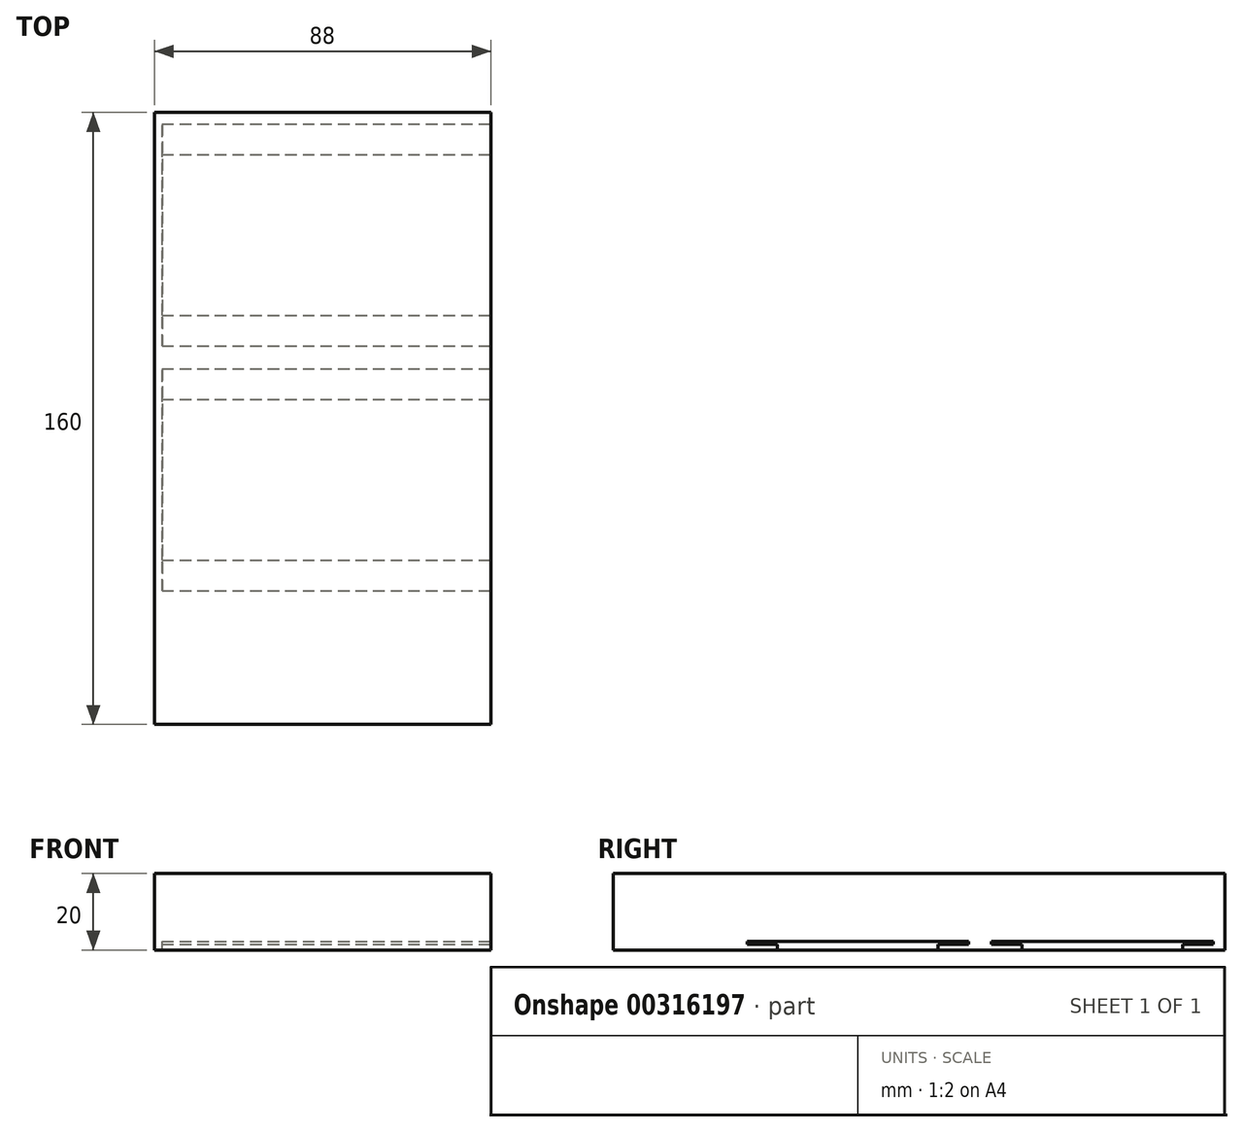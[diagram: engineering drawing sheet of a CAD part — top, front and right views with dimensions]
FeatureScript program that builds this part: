
annotation { "Feature Type Name" : "Feature", "Feature Type Description" : "" }
export const myFeature = defineFeature(function(context is Context, id is Id, definition is map)
    precondition{}
    {
        {
            var Q0;
            Q0=qCreatedBy(makeId("Top.planeOp"),FACE);
            var sketch = newSketch(context, id + "F0", { "sketchPlane" : qUnion([Q0])});
            skLineSegment(sketch, "E0.bottom", {"start": v(0, 0) * mm, "end": v(88, 0) * mm});
            skLineSegment(sketch, "E0.top", {"start": v(0, 160) * mm, "end": v(88, 160) * mm});
            skLineSegment(sketch, "E0.left", {"start": v(0, 0) * mm, "end": v(0, 160) * mm});
            skLineSegment(sketch, "E0.right", {"start": v(88, 0) * mm, "end": v(88, 160) * mm});
            skSolve(sketch);
        }
        {
            var Q0;
            Q0 = qSketchRegion(id + "F0", true);
            extrude(context, id + "F1", {"entities" : qUnion([Q0]), "depth" : 20 * mm});
        }
        {
            var Q0;
            Q0=makeQuery(id+"F1.opExtrude","SWEPT_FACE",FACE,{"disambiguationData":[OSD([sQuery(id+"F0.wireOp",EDGE,"E0.right")])]});
            var sketch = newSketch(context, id + "F2", { "sketchPlane" : qUnion([Q0])});
            skLineSegment(sketch, "E1", {"start": v(149, 0) * mm, "end": v(149, 1.5) * mm});
            skLineSegment(sketch, "E2", {"start": v(149, 1.5) * mm, "end": v(157, 1.5) * mm});
            skLineSegment(sketch, "E3", {"start": v(157, 1.5) * mm, "end": v(157, 2.3) * mm});
            skLineSegment(sketch, "E4", {"start": v(157, 2.3) * mm, "end": v(99, 2.3) * mm});
            skLineSegment(sketch, "E5", {"start": v(99, 2.3) * mm, "end": v(99, 1.5) * mm});
            skLineSegment(sketch, "E6", {"start": v(99, 1.5) * mm, "end": v(107, 1.5) * mm});
            skLineSegment(sketch, "E7", {"start": v(107, 1.5) * mm, "end": v(107, 0) * mm});
            skLineSegment(sketch, "E8", {"start": v(107, 0) * mm, "end": v(149, 0) * mm});
            skLineSegment(sketch, "E9", {"start": v(128, 0) * mm, "end": v(128, 2.3) * mm, "construction": true});
            skLineSegment(sketch, "E10.1.0.0", {"start": v(93, 2.3) * mm, "end": v(35, 2.3) * mm});
            skLineSegment(sketch, "E10.1.0.1", {"start": v(85, 1.5) * mm, "end": v(93, 1.5) * mm});
            skLineSegment(sketch, "E10.1.0.2", {"start": v(93, 1.5) * mm, "end": v(93, 2.3) * mm});
            skLineSegment(sketch, "E10.1.0.3", {"start": v(85, 0) * mm, "end": v(85, 1.5) * mm});
            skLineSegment(sketch, "E10.1.0.4", {"start": v(43, 0) * mm, "end": v(85, 0) * mm});
            skLineSegment(sketch, "E10.1.0.5", {"start": v(43, 1.5) * mm, "end": v(43, 0) * mm});
            skLineSegment(sketch, "E10.1.0.6", {"start": v(35, 1.5) * mm, "end": v(43, 1.5) * mm});
            skLineSegment(sketch, "E10.1.0.7", {"start": v(35, 2.3) * mm, "end": v(35, 1.5) * mm});
            skLineSegment(sketch, "E10.direction1", {"start": v(35, 2.3) * mm, "end": v(99, 2.3) * mm, "construction": true});
            skSolve(sketch);
        }
        {
            var Q0;
            Q0 = qSketchRegion(id + "F2", true);
            extrude(context, id + "F3", {"entities" : qUnion([Q0]), "operationType" : NewBodyOperationType.REMOVE, "oppositeDirection" : true, "depth" : 86 * mm});
        }
    });
